# Revit family: Access_Controller-I_O-Vicon-VAX-Control_Box
name_source: partatom
category: Security Devices
revit_build: Autodesk Revit 2014 (Build: 20140709_2115(x64)
units: mm (PartAtom-declared; Revit-internal decimal feet)

## types (1)
- VAX-IO-STR
    Apparent Load = 15 VA
    Assembly Code = E1010110
    Connector Description = Connector for Electrical Power
    Connector Type = PoE/Network: RJ-45 CAT 5
    Default Elevation = 1219 mm
    Description = Input/Output Controller; Includes 8 input/output expansion modules, accepts up to 7 expanders
    Housing Material = Metal - Vicon - Cast Aluminum - Black
    Load Classification = Power
    Manufacturer = Vicon Industries
    Model = VAX-IO-STR
    Number of Poles = 1
    Operating Humidity = 10% to 90% Relative Humidity, Non-Condensing
    Operating Temperature = 32 to 122 Degrees Fahrenheit
    Power Factor = 1
    Product Documentation Link = http://www.vicon-security.com
    Product Page URL = http://www.vicon-security.com
    URL = http://www.vicon-security.com
    Voltage = 12 V
    Watts = 15 W
    Weight = 4.10 lb

## geometry (parser evidence)
native form markers: Sweep x1
no freeform markers — native parametric forms only
